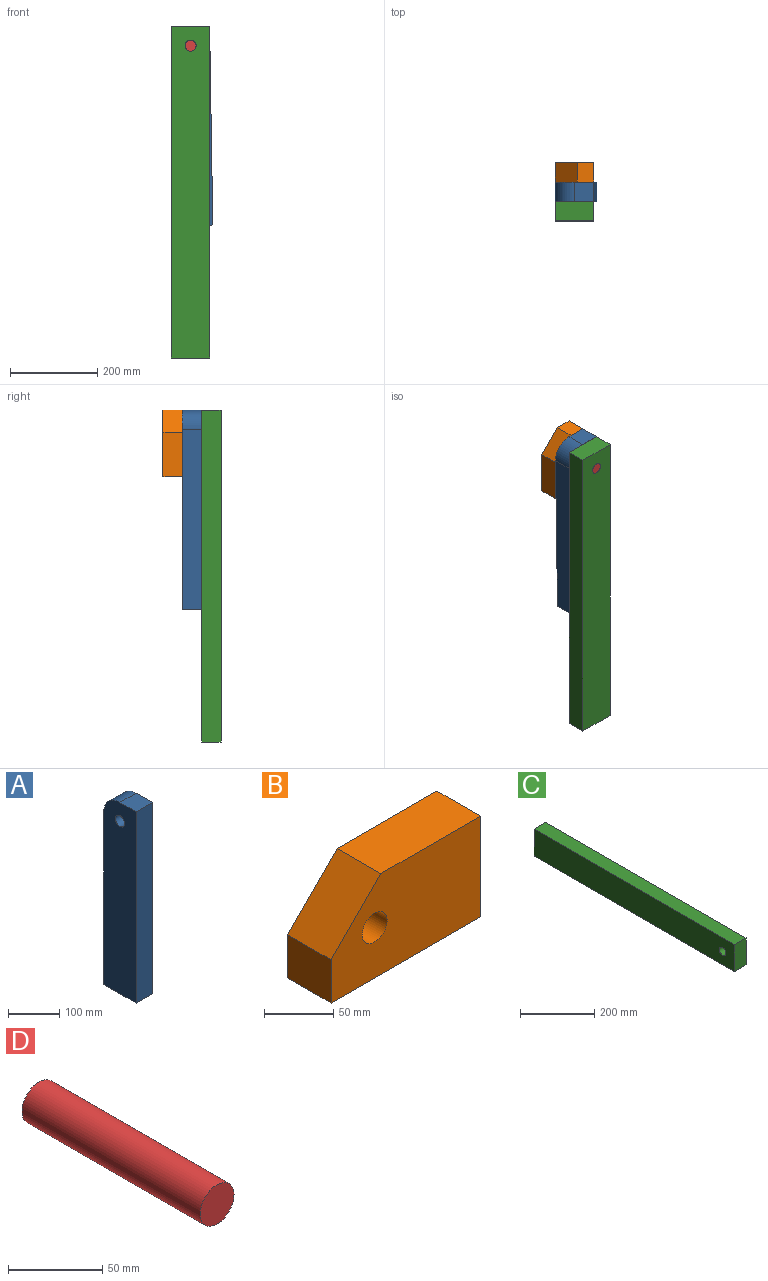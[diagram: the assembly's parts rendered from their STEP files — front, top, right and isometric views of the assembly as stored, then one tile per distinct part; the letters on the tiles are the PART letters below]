
ASSEMBLY  parts=4 mates=5
PART A: 8 faces, bbox 44.5x88.9x457.2 mm
  f0: plane 44.45x44.45mm, normal (0,0,1), area 1975.8mm2, adj f1,f5,f6,f7
  f1: plane 457.2x44.45mm, normal (0,-1,0), area 20322.5mm2, adj f0,f2,f6,f7
  f2: plane 88.9x44.45mm, normal (0,0,-1), area 3951.6mm2, adj f1,f3,f6,f7
  f3: plane 412.75x44.45mm, normal (0,1,0), area 18346.7mm2, adj f2,f5,f6,f7
  f4: cylinder r=12.7mm len=44.45mm, axis (-1,0,0), area 3547mm2, adj f6,f7
  f5: cylinder r=44.45mm len=44.45mm, axis (-1,0,0), area 3103.6mm2, adj f0,f3,f6,f7
  f6: plane 457.2x88.9mm, normal (1,0,0), area 39714.4mm2, adj f0,f1,f2,f3,f4,f5
  f7: plane 457.2x88.9mm, normal (-1,0,0), area 39714.4mm2, adj f0,f1,f2,f3,f4,f5
PART B: 8 faces, bbox 152.4x44.5x88.9 mm
  f0: plane 101.6x44.45mm, normal (0,0,1), area 4516.1mm2, adj f1,f4,f6,f7
  f1: plane 50.8x50.8mm, normal (-0.71,0,0.71), area 3193.4mm2, adj f0,f2,f6,f7
  f2: plane 44.45x38.1mm, normal (-1,0,0), area 1693.5mm2, adj f1,f3,f6,f7
  f3: plane 152.4x44.45mm, normal (0,0,-1), area 6774.2mm2, adj f2,f4,f6,f7
  f4: plane 88.9x44.45mm, normal (1,0,0), area 3951.6mm2, adj f0,f3,f6,f7
  f5: cylinder r=12.7mm len=44.45mm, axis (0,1,0), area 3547mm2, adj f6,f7
  f6: plane 152.4x88.9mm, normal (0,-1,0), area 11751.3mm2, adj f0,f1,f2,f3,f4,f5
  f7: plane 152.4x88.9mm, normal (0,1,0), area 11751.3mm2, adj f0,f1,f2,f3,f4,f5
PART C: 7 faces, bbox 44.5x762x88.9 mm
  f0: plane 762x88.9mm, normal (-1,0,0), area 67235.1mm2, adj f1,f3,f4,f5,f6
  f1: plane 762x44.45mm, normal (0,0,-1), area 33870.9mm2, adj f0,f2,f4,f5
  f2: plane 762x88.9mm, normal (1,0,0), area 67235.1mm2, adj f1,f3,f4,f5,f6
  f3: plane 762x44.45mm, normal (0,0,1), area 33870.9mm2, adj f0,f2,f4,f5
  f4: plane 88.9x44.45mm, normal (0,-1,0), area 3951.6mm2, adj f0,f1,f2,f3
  f5: plane 88.9x44.45mm, normal (0,1,0), area 3951.6mm2, adj f0,f1,f2,f3
  f6: cylinder r=12.7mm len=44.45mm, axis (1,0,0), area 3547mm2, adj f0,f2
PART D: 3 faces, bbox 25.4x133.4x25.4 mm
  f0: cylinder r=12.7mm len=133.35mm, axis (0,1,0), area 10640.9mm2, adj f1,f2
  f1: plane 25.4x25.4mm, normal (0,-1,0), area 506.7mm2, adj f0
  f2: plane 25.4x25.4mm, normal (0,1,0), area 506.7mm2, adj f0
PLACE A rot(axis=(-0.01,-0.01,1),90deg) t=(250.43,41.03,650.41)mm
PLACE B rot(axis=(0.71,0,-0.71),180deg) t=(251.15,85.48,649.7)mm
PLACE C rot(axis=(-0.58,-0.58,0.58),120deg) t=(251.15,-3.42,-112.3)mm
PLACE D t=(206.7,129.93,605.25)mm
MATE revolute B.f5 <-> D.f0  axis (0,1,0) through (206.7,129.93,605.25)mm
MATE revolute A.f4 <-> D.f0  axis (0,-1,0) through (206.7,63.26,605.25)mm
MATE cylindrical D.f0 <-> C.f6  axis (0,1,0) through (206.7,-3.42,605.25)mm
MATE planar C.f3 <-> B.f0  axis (-1,0,0) through (162.25,18.81,268.7)mm
MATE fastened D.f0 <-> C.f6  axis (0,-1,0) through (206.7,-3.42,605.25)mm
